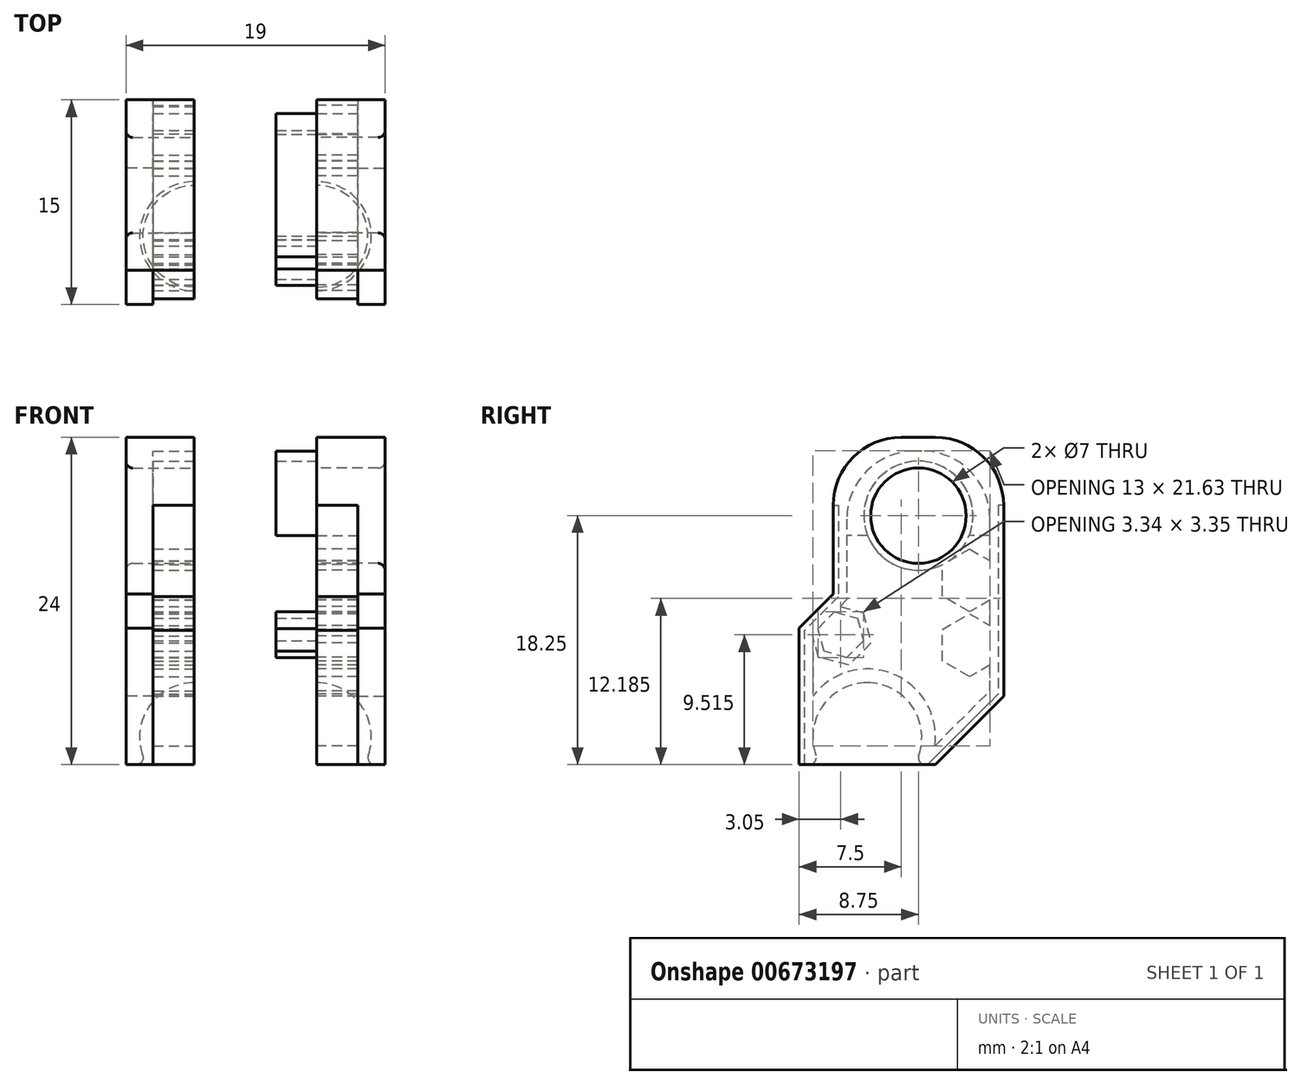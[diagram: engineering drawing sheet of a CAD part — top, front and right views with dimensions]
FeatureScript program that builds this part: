
annotation { "Feature Type Name" : "Feature", "Feature Type Description" : "" }
export const myFeature = defineFeature(function(context is Context, id is Id, definition is map)
    precondition{}
    {
        {
            var Q0;
            Q0=qCreatedBy(makeId("Right.planeOp"),FACE);
            var sketch = newSketch(context, id + "F0", { "sketchPlane" : qUnion([Q0])});
            skLineSegment(sketch, "E0.bottom", {"start": v(0, 0) * mm, "end": v(10, 0) * mm});
            skLineSegment(sketch, "E0.left", {"start": v(0, 0) * mm, "end": v(0, 10) * mm});
            skLineSegment(sketch, "E1.right", {"start": v(15, 5) * mm, "end": v(15, 20) * mm});
            skLineSegment(sketch, "E2", {"start": v(15, 5) * mm, "end": v(10, 0) * mm});
            skLineSegment(sketch, "E3", {"start": v(2.5, 12.5) * mm, "end": v(0, 10) * mm});
            skLineSegment(sketch, "E4", {"start": v(2.5, 12.5) * mm, "end": v(2.5, 20) * mm});
            skLineSegment(sketch, "E5.top", {"start": v(2.5, 24) * mm, "end": v(15, 24) * mm});
            skLineSegment(sketch, "E5.left", {"start": v(2.5, 20) * mm, "end": v(2.5, 24) * mm});
            skLineSegment(sketch, "E5.right", {"start": v(15, 20) * mm, "end": v(15, 24) * mm});
            skSolve(sketch);
        }
        {
            var Q0;
            Q0=qSketchRegion(id+"F0",true);
            extrude(context, id + "F1", {"entities" : qUnion([Q0]), "depth" : 5 * mm});
        }
        {
            var Q0;
            Q0=makeQuery(id+"F1.opExtrude","CAP_FACE",FACE,{"disambiguationData":[OSD([sQuery(id+"F0.wireOp",EDGE,"E0.bottom"),sQuery(id+"F0.wireOp",EDGE,"E0.left"),sQuery(id+"F0.wireOp",EDGE,"E1.top"),sQuery(id+"F0.wireOp",EDGE,"E1.right"),sQuery(id+"F0.wireOp",EDGE,"E2"),sQuery(id+"F0.wireOp",EDGE,"E3"),sQuery(id+"F0.wireOp",EDGE,"E4"),sQuery(id+"F0.wireOp",EDGE,"LedBFlpj-Cklq-8Npn-dqWy-Sleq267MBf9Z")])],"isStart":false});
            var sketch = newSketch(context, id + "F2", { "sketchPlane" : qUnion([Q0])});
            skLineSegment(sketch, "E6", {"start": v(5, 0) * mm, "end": v(5, 2) * mm, "construction": true});
            skArc(sketch, "E7", {"start": v(5, 6) * mm, "mid": v(1, 2) * mm, "end": v(5, -2) * mm});
            skLineSegment(sketch, "E8", {"start": v(5, 6) * mm, "end": v(5, -2) * mm});
            skSolve(sketch);
        }
        {
            var Q0;
            Q0=qSketchRegion(id+"F2",true);
            var Q1;
            Q1=sQuery(id+"F2.wireOp",EDGE,"E8");
            revolve(context, id + "F3", {"operationType" : NewBodyOperationType.REMOVE, "entities" : qUnion([Q0]), "axis" : qUnion([Q1]), "revolveType" : RevolveType.FULL, "oppositeDirection" : true});
        }
        {
            var Q0;
            Q0=makeQuery(id+"F1.opExtrude","CAP_FACE",FACE,{"disambiguationData":[OSD([sQuery(id+"F0.wireOp",EDGE,"E0.bottom"),sQuery(id+"F0.wireOp",EDGE,"E0.left"),sQuery(id+"F0.wireOp",EDGE,"E1.right"),sQuery(id+"F0.wireOp",EDGE,"E2"),sQuery(id+"F0.wireOp",EDGE,"E3"),sQuery(id+"F0.wireOp",EDGE,"E4"),sQuery(id+"F0.wireOp",EDGE,"E5.top"),sQuery(id+"F0.wireOp",EDGE,"E5.left"),sQuery(id+"F0.wireOp",EDGE,"E5.right")])],"isStart":false});
            var sketch = newSketch(context, id + "F4", { "sketchPlane" : qUnion([Q0])});
            skCircle(sketch, "E9", {"center": v(8.75, 18.25) * mm, "radius": 3.5 * mm});
            skPoint(sketch, "E9.centerSnap0", {"position": v(2.5, 18.25) * mm});
            skPoint(sketch, "E9.centerSnap1", {"position": v(8.75, 24) * mm});
            skSolve(sketch);
        }
        {
            var Q0;
            Q0=qSketchRegion(id+"F4",true);
            extrude(context, id + "F5", {"entities" : qUnion([Q0]), "operationType" : NewBodyOperationType.REMOVE, "oppositeDirection" : true, "depth" : 25 * mm});
        }
        {
            var Q0;
            Q0=makeQuery(id+"F1.opExtrude","CAP_FACE",FACE,{"disambiguationData":[OSD([sQuery(id+"F0.wireOp",EDGE,"E0.bottom"),sQuery(id+"F0.wireOp",EDGE,"E0.left"),sQuery(id+"F0.wireOp",EDGE,"E1.right"),sQuery(id+"F0.wireOp",EDGE,"E2"),sQuery(id+"F0.wireOp",EDGE,"E3"),sQuery(id+"F0.wireOp",EDGE,"E4"),sQuery(id+"F0.wireOp",EDGE,"E5.top"),sQuery(id+"F0.wireOp",EDGE,"E5.left"),sQuery(id+"F0.wireOp",EDGE,"E5.right")])],"isStart":false});
            var sketch = newSketch(context, id + "F6", { "sketchPlane" : qUnion([Q0])});
            skLineSegment(sketch, "E10.0", {"start": v(1, 9.59) * mm, "end": v(1, 5) * mm});
            skLineSegment(sketch, "E10.1", {"start": v(3.5, 12.09) * mm, "end": v(1, 9.59) * mm});
            skLineSegment(sketch, "E10.2", {"start": v(9.96, 1.37) * mm, "end": v(14, 5.41) * mm});
            skLineSegment(sketch, "E10.3", {"start": v(14, 5.41) * mm, "end": v(14, 23) * mm});
            skLineSegment(sketch, "E10.4", {"start": v(14, 23) * mm, "end": v(3.5, 23) * mm});
            skArc(sketch, "E10.5", {"start": v(1, 5) * mm, "mid": v(6.88, 6.64) * mm, "end": v(9.96, 1.37) * mm});
            skLineSegment(sketch, "E10.6", {"start": v(3.5, 23) * mm, "end": v(3.5, 12.09) * mm});
            skCircle(sketch, "E11.cCircle", {"center": v(12.5, 8.75) * mm, "radius": 1.5 * mm, "construction": true});
            skLineSegment(sketch, "E11.0", {"start": v(14, 9.61) * mm, "end": v(14, 7.88) * mm});
            skLineSegment(sketch, "E11.1", {"start": v(14, 7.88) * mm, "end": v(12.5, 7.01) * mm});
            skLineSegment(sketch, "E11.2", {"start": v(12.5, 7.01) * mm, "end": v(11, 7.88) * mm});
            skLineSegment(sketch, "E11.3", {"start": v(11, 7.88) * mm, "end": v(11, 9.61) * mm});
            skLineSegment(sketch, "E11.4", {"start": v(11, 9.61) * mm, "end": v(12.5, 10.48) * mm});
            skLineSegment(sketch, "E11.5", {"start": v(12.5, 10.48) * mm, "end": v(14, 9.61) * mm});
            skPoint(sketch, "E11.0.midPoint", {"position": v(14, 8.75) * mm});
            skCircle(sketch, "E12.cCircle", {"center": v(3.05, 9.52) * mm, "radius": 1.5 * mm, "construction": true});
            skLineSegment(sketch, "E12.0", {"start": v(1.38, 9.96) * mm, "end": v(2.6, 11.19) * mm});
            skLineSegment(sketch, "E12.1", {"start": v(2.6, 11.19) * mm, "end": v(4.28, 10.74) * mm});
            skLineSegment(sketch, "E12.2", {"start": v(4.28, 10.74) * mm, "end": v(4.72, 9.07) * mm});
            skLineSegment(sketch, "E12.3", {"start": v(4.72, 9.07) * mm, "end": v(3.5, 7.84) * mm});
            skLineSegment(sketch, "E12.4", {"start": v(3.5, 7.84) * mm, "end": v(1.83, 8.3) * mm});
            skLineSegment(sketch, "E12.5", {"start": v(1.83, 8.3) * mm, "end": v(1.38, 9.96) * mm});
            skPoint(sketch, "E12.0.midPoint", {"position": v(2, 10.58) * mm});
            skCircle(sketch, "E13.cCircle", {"center": v(12.5, 13.5) * mm, "radius": 1.5 * mm, "construction": true});
            skLineSegment(sketch, "E13.0", {"start": v(14, 14.37) * mm, "end": v(14, 12.63) * mm});
            skLineSegment(sketch, "E13.1", {"start": v(14, 12.63) * mm, "end": v(12.5, 11.77) * mm});
            skLineSegment(sketch, "E13.2", {"start": v(12.5, 11.77) * mm, "end": v(11, 12.63) * mm});
            skLineSegment(sketch, "E13.3", {"start": v(11, 12.63) * mm, "end": v(11, 14.37) * mm});
            skLineSegment(sketch, "E13.4", {"start": v(11, 14.37) * mm, "end": v(12.5, 15.23) * mm});
            skLineSegment(sketch, "E13.5", {"start": v(12.5, 15.23) * mm, "end": v(14, 14.37) * mm});
            skPoint(sketch, "E13.0.midPoint", {"position": v(14, 13.5) * mm});
            skCircle(sketch, "E14", {"center": v(8.75, 18.25) * mm, "radius": 4 * mm});
            skCircle(sketch, "E15.cCircle", {"center": v(12.5, 8.75) * mm, "radius": 2 * mm, "construction": true});
            skLineSegment(sketch, "E15.1", {"start": v(14, 7.3) * mm, "end": v(12.5, 6.44) * mm});
            skLineSegment(sketch, "E15.2", {"start": v(12.5, 6.44) * mm, "end": v(10.5, 7.6) * mm});
            skLineSegment(sketch, "E15.3", {"start": v(10.5, 7.6) * mm, "end": v(10.5, 9.9) * mm});
            skLineSegment(sketch, "E15.4", {"start": v(10.5, 9.9) * mm, "end": v(12.5, 11.06) * mm});
            skLineSegment(sketch, "E15.5", {"start": v(12.5, 11.06) * mm, "end": v(14, 10.19) * mm});
            skPoint(sketch, "E15.0.midPoint", {"position": v(14.5, 8.75) * mm});
            skCircle(sketch, "E16.cCircle", {"center": v(12.5, 13.5) * mm, "radius": 2 * mm, "construction": true});
            skLineSegment(sketch, "E16.1", {"start": v(14, 12.06) * mm, "end": v(12.5, 11.2) * mm});
            skLineSegment(sketch, "E16.2", {"start": v(12.5, 11.2) * mm, "end": v(10.5, 12.35) * mm});
            skLineSegment(sketch, "E16.3", {"start": v(10.5, 12.35) * mm, "end": v(10.5, 14.65) * mm});
            skLineSegment(sketch, "E16.4", {"start": v(10.5, 14.65) * mm, "end": v(12.5, 15.8) * mm});
            skLineSegment(sketch, "E16.5", {"start": v(12.5, 15.8) * mm, "end": v(14, 14.94) * mm});
            skPoint(sketch, "E16.0.midPoint", {"position": v(14.5, 13.5) * mm});
            skArc(sketch, "E17.cCircle", {"start": v(1.06, 9.64) * mm, "mid": v(4.47, 8.1) * mm, "end": v(2.93, 11.51) * mm, "construction": true});
            skLineSegment(sketch, "E17.1", {"start": v(3.01, 11.6) * mm, "end": v(4.68, 11.15) * mm});
            skLineSegment(sketch, "E17.2", {"start": v(4.68, 11.15) * mm, "end": v(5.28, 8.92) * mm});
            skLineSegment(sketch, "E17.3", {"start": v(5.28, 8.92) * mm, "end": v(3.65, 7.29) * mm});
            skLineSegment(sketch, "E17.4", {"start": v(3.65, 7.29) * mm, "end": v(1.42, 7.88) * mm});
            skLineSegment(sketch, "E17.5", {"start": v(1.42, 7.88) * mm, "end": v(1, 9.44) * mm});
            skPoint(sketch, "E17.0.midPoint", {"position": v(1.64, 10.93) * mm});
            skPoint(sketch, "E18.orphan", {"position": v(0.82, 10.11) * mm});
            skPoint(sketch, "E19.orphan", {"position": v(2.45, 11.75) * mm});
            skPoint(sketch, "E20.orphan", {"position": v(14.5, 7.6) * mm});
            skPoint(sketch, "E21.orphan", {"position": v(14.5, 9.9) * mm});
            skPoint(sketch, "E22.orphan", {"position": v(14.5, 12.35) * mm});
            skPoint(sketch, "E23.orphan", {"position": v(14.5, 14.65) * mm});
            skSolve(sketch);
        }
        {
            var Q0;
            {var subQ15=sQuery(id+"F6.wireOp",EDGE,"E10.2");Q0=makeQuery(id+"F6.imprint","IMPRINT",FACE,{"disambiguationData":[TD([[makeQuery(id+"F6.imprint","IMPRINT",EDGE,{"derivedFrom":subQ15}),1.0]])]});}
            var Q1;
            Q1=makeQuery(id+"F6.imprint","IMPRINT",FACE,{"disambiguationData":[TD([[makeQuery(id+"F6.imprint","IMPRINT",EDGE,{"derivedFrom":sQuery(id+"F6.wireOp",EDGE,"E12.0")}),-1.0]])]});
            var Q2;
            Q2=makeQuery(id+"F6.imprint","IMPRINT",FACE,{"disambiguationData":[TD([[makeQuery(id+"F6.imprint","IMPRINT",EDGE,{"derivedFrom":sQuery(id+"F6.wireOp",EDGE,"E11.0")}),-1.0]])]});
            var Q3;
            Q3=makeQuery(id+"F6.imprint","IMPRINT",FACE,{"disambiguationData":[TD([[makeQuery(id+"F6.imprint","IMPRINT",EDGE,{"derivedFrom":sQuery(id+"F6.wireOp",EDGE,"E13.0")}),-1.0]])]});
            extrude(context, id + "F7", {"entities" : qUnion([Q0, Q1, Q2, Q3]), "operationType" : NewBodyOperationType.REMOVE, "oppositeDirection" : true, "depth" : 3 * mm});
        }
        {
            var Q0;
            Q0=qCreatedBy(makeId("Right.planeOp"),FACE);
            cPlane(context, id + "F8", {"entities" : qUnion([Q0]), "cplaneType" : CPlaneType.OFFSET, "offset" : 9.5 * mm, "width" : 150 * mm, "height" : 150 * mm});
        }
        {
            var Q0;
            Q0=makeQuery(id+"F1.opExtrude","SWEPT_EDGE",EDGE,{"disambiguationData":[OSD([sQuery(id+"F0.wireOp",EDGE,"E5.top"),sQuery(id+"F0.wireOp",EDGE,"E5.left")])]});
            var Q1;
            Q1=makeQuery(id+"F1.opExtrude","SWEPT_EDGE",EDGE,{"disambiguationData":[OSD([sQuery(id+"F0.wireOp",EDGE,"E5.top"),sQuery(id+"F0.wireOp",EDGE,"E5.right")])]});
            var Q2;
            Q2=makeQuery(id+"F7.boolean.opBoolean","COPY",EDGE,{"derivedFrom":makeQuery(id+"F7.opExtrude","SWEPT_EDGE",EDGE,{"disambiguationData":[OSD([sQuery(id+"F6.wireOp",EDGE,"E10.4"),sQuery(id+"F6.wireOp",EDGE,"E10.6")])]})});
            var Q3;
            Q3=makeQuery(id+"F7.boolean.opBoolean","COPY",EDGE,{"derivedFrom":makeQuery(id+"F7.opExtrude","SWEPT_EDGE",EDGE,{"disambiguationData":[OSD([sQuery(id+"F6.wireOp",EDGE,"E10.3"),sQuery(id+"F6.wireOp",EDGE,"E10.4")])]})});
            fillet(context, id + "F9", {"entities" : qUnion([Q0, Q1, Q2, Q3]), "radius" : 5 * mm, "tangentPropagation" : true, "allowEdgeOverflow" : false});
        }
        {
            var Q0;
            Q0=makeQuery(id+"F1.opExtrude","SWEPT_BODY",BODY,{"disambiguationData":[OSD([sQuery(id+"F0.wireOp",EDGE,"E0.bottom"),sQuery(id+"F0.wireOp",EDGE,"E0.left"),sQuery(id+"F0.wireOp",EDGE,"E1.right"),sQuery(id+"F0.wireOp",EDGE,"E2"),sQuery(id+"F0.wireOp",EDGE,"E3"),sQuery(id+"F0.wireOp",EDGE,"E4"),sQuery(id+"F0.wireOp",EDGE,"E5.top"),sQuery(id+"F0.wireOp",EDGE,"E5.left"),sQuery(id+"F0.wireOp",EDGE,"E5.right")])]});
            var Q1;
            Q1=qCreatedBy(id+"F8.planeOp",FACE);
            mirror(context, id + "F10", {"entities" : qUnion([Q0]), "mirrorPlane" : qUnion([Q1])});
        }
        {
            var Q0;
            Q0=makeQuery(id+"F10.opPattern","COPY",FACE,{"derivedFrom":makeQuery(id+"F7.boolean.opBoolean","COPY",FACE,{"derivedFrom":makeQuery(id+"F7.opExtrude","CAP_FACE",FACE,{"disambiguationData":[OSD([sQuery(id+"F6.wireOp",EDGE,"E11.0"),sQuery(id+"F6.wireOp",EDGE,"E11.1"),sQuery(id+"F6.wireOp",EDGE,"E11.2"),sQuery(id+"F6.wireOp",EDGE,"E11.3"),sQuery(id+"F6.wireOp",EDGE,"E11.4"),sQuery(id+"F6.wireOp",EDGE,"E11.5")])],"isStart":false})}),"instanceName":"1"});
            var Q1;
            Q1=makeQuery(id+"F10.opPattern","COPY",FACE,{"derivedFrom":makeQuery(id+"F7.boolean.opBoolean","COPY",FACE,{"derivedFrom":makeQuery(id+"F7.opExtrude","CAP_FACE",FACE,{"disambiguationData":[OSD([sQuery(id+"F6.wireOp",EDGE,"E13.0"),sQuery(id+"F6.wireOp",EDGE,"E13.1"),sQuery(id+"F6.wireOp",EDGE,"E13.2"),sQuery(id+"F6.wireOp",EDGE,"E13.3"),sQuery(id+"F6.wireOp",EDGE,"E13.4"),sQuery(id+"F6.wireOp",EDGE,"E13.5")])],"isStart":false})}),"instanceName":"1"});
            var Q2;
            Q2=makeQuery(id+"F10.opPattern","COPY",FACE,{"derivedFrom":makeQuery(id+"F7.boolean.opBoolean","COPY",FACE,{"derivedFrom":makeQuery(id+"F7.opExtrude","CAP_FACE",FACE,{"disambiguationData":[OSD([sQuery(id+"F6.wireOp",EDGE,"E12.0"),sQuery(id+"F6.wireOp",EDGE,"E12.1"),sQuery(id+"F6.wireOp",EDGE,"E12.2"),sQuery(id+"F6.wireOp",EDGE,"E12.3"),sQuery(id+"F6.wireOp",EDGE,"E12.4"),sQuery(id+"F6.wireOp",EDGE,"E12.5")])],"isStart":false})}),"instanceName":"1"});
            extrude(context, id + "F11", {"entities" : qUnion([Q0, Q1, Q2]), "operationType" : NewBodyOperationType.ADD, "depth" : 6 * mm});
        }
        {
            var Q0;
            Q0=makeQuery(id+"F10.opPattern","COPY",FACE,{"derivedFrom":makeQuery(id+"F7.boolean.opBoolean","COPY",FACE,{"derivedFrom":makeQuery(id+"F7.opExtrude","CAP_FACE",FACE,{"disambiguationData":[OSD([sQuery(id+"F6.wireOp",EDGE,"E10.0"),sQuery(id+"F6.wireOp",EDGE,"E10.1"),sQuery(id+"F6.wireOp",EDGE,"E10.2"),sQuery(id+"F6.wireOp",EDGE,"E10.3"),sQuery(id+"F6.wireOp",EDGE,"E10.4"),sQuery(id+"F6.wireOp",EDGE,"E10.5"),sQuery(id+"F6.wireOp",EDGE,"E10.6"),sQuery(id+"F6.wireOp",EDGE,"E14"),sQuery(id+"F6.wireOp",EDGE,"E15.1"),sQuery(id+"F6.wireOp",EDGE,"E15.2"),sQuery(id+"F6.wireOp",EDGE,"E15.3"),sQuery(id+"F6.wireOp",EDGE,"E15.4"),sQuery(id+"F6.wireOp",EDGE,"E15.5"),sQuery(id+"F6.wireOp",EDGE,"E16.1"),sQuery(id+"F6.wireOp",EDGE,"E16.2"),sQuery(id+"F6.wireOp",EDGE,"E16.3"),sQuery(id+"F6.wireOp",EDGE,"E16.4"),sQuery(id+"F6.wireOp",EDGE,"E16.5"),sQuery(id+"F6.wireOp",EDGE,"E17.1"),sQuery(id+"F6.wireOp",EDGE,"E17.2"),sQuery(id+"F6.wireOp",EDGE,"E17.3"),sQuery(id+"F6.wireOp",EDGE,"E17.4"),sQuery(id+"F6.wireOp",EDGE,"E17.5")])],"isStart":false})}),"instanceName":"1"});
            var sketch = newSketch(context, id + "F12", { "sketchPlane" : qUnion([Q0])});
            skLineSegment(sketch, "E24", {"start": v(-14, 15.8) * mm, "end": v(-14, 16.8) * mm, "construction": true});
            skLineSegment(sketch, "E25", {"start": v(-14, 16.8) * mm, "end": v(-12.48, 16.8) * mm});
            skLineSegment(sketch, "E26", {"start": v(-12.48, 16.8) * mm, "end": v(-3.5, 16.8) * mm});
            skSolve(sketch);
        }
        {
            var Q0;
            {var subQ14=sQuery(id+"F12.wireOp",EDGE,"E25");Q0=makeQuery(id+"F12.imprint","IMPRINT",FACE,{"disambiguationData":[TD([[makeQuery(id+"F12.imprint","IMPRINT",EDGE,{"derivedFrom":subQ14}),1.0]])]});}
            extrude(context, id + "F13", {"entities" : qUnion([Q0]), "operationType" : NewBodyOperationType.ADD, "depth" : 6 * mm});
        }
        {
            var Q0;
            Q0=makeQuery(id+"F5.boolean.opBoolean","INTERSECT",EDGE,{"derivedFrom":[makeQuery(id+"F1.opExtrude","CAP_FACE",FACE,{"disambiguationData":[OSD([sQuery(id+"F0.wireOp",EDGE,"E0.bottom"),sQuery(id+"F0.wireOp",EDGE,"E0.left"),sQuery(id+"F0.wireOp",EDGE,"E1.right"),sQuery(id+"F0.wireOp",EDGE,"E2"),sQuery(id+"F0.wireOp",EDGE,"E3"),sQuery(id+"F0.wireOp",EDGE,"E4"),sQuery(id+"F0.wireOp",EDGE,"E5.top"),sQuery(id+"F0.wireOp",EDGE,"E5.left"),sQuery(id+"F0.wireOp",EDGE,"E5.right")])],"isStart":true}),makeQuery(id+"F5.opExtrude","SWEPT_FACE",FACE,{"disambiguationData":[OSD([sQuery(id+"F4.wireOp",EDGE,"E9")])]})]});
            var Q1;
            Q1=makeQuery(id+"F10.opPattern","COPY",EDGE,{"derivedFrom":makeQuery(id+"F5.boolean.opBoolean","INTERSECT",EDGE,{"derivedFrom":[makeQuery(id+"F1.opExtrude","CAP_FACE",FACE,{"disambiguationData":[OSD([sQuery(id+"F0.wireOp",EDGE,"E0.bottom"),sQuery(id+"F0.wireOp",EDGE,"E0.left"),sQuery(id+"F0.wireOp",EDGE,"E1.right"),sQuery(id+"F0.wireOp",EDGE,"E2"),sQuery(id+"F0.wireOp",EDGE,"E3"),sQuery(id+"F0.wireOp",EDGE,"E4"),sQuery(id+"F0.wireOp",EDGE,"E5.top"),sQuery(id+"F0.wireOp",EDGE,"E5.left"),sQuery(id+"F0.wireOp",EDGE,"E5.right")])],"isStart":true}),makeQuery(id+"F5.opExtrude","SWEPT_FACE",FACE,{"disambiguationData":[OSD([sQuery(id+"F4.wireOp",EDGE,"E9")])]})]}),"instanceName":"1"});
            var Q2;
            Q2=makeQuery(id+"F10.opPattern","COPY",EDGE,{"derivedFrom":makeQuery(id+"F3.boolean.opBoolean","INTERSECT",EDGE,{"derivedFrom":[makeQuery(id+"F1.opExtrude","SWEPT_FACE",FACE,{"disambiguationData":[OSD([sQuery(id+"F0.wireOp",EDGE,"E0.bottom")])]}),makeQuery(id+"F3.opRevolve","SWEPT_FACE",FACE,{"disambiguationData":[OSD([sQuery(id+"F2.wireOp",EDGE,"E7")])]})]}),"instanceName":"1"});
            var Q3;
            Q3=makeQuery(id+"F3.boolean.opBoolean","INTERSECT",EDGE,{"derivedFrom":[makeQuery(id+"F1.opExtrude","SWEPT_FACE",FACE,{"disambiguationData":[OSD([sQuery(id+"F0.wireOp",EDGE,"E0.bottom")])]}),makeQuery(id+"F3.opRevolve","SWEPT_FACE",FACE,{"disambiguationData":[OSD([sQuery(id+"F2.wireOp",EDGE,"E7")])]})]});
            fillet(context, id + "F14", {"entities" : qUnion([Q0, Q1, Q2, Q3]), "radius" : .5 * mm, "tangentPropagation" : true, "allowEdgeOverflow" : false});
        }
        {
            var Q0;
            Q0=makeQuery(id+"F1.opExtrude","CAP_FACE",FACE,{"disambiguationData":[OSD([sQuery(id+"F0.wireOp",EDGE,"E0.bottom"),sQuery(id+"F0.wireOp",EDGE,"E0.left"),sQuery(id+"F0.wireOp",EDGE,"E1.right"),sQuery(id+"F0.wireOp",EDGE,"E2"),sQuery(id+"F0.wireOp",EDGE,"E3"),sQuery(id+"F0.wireOp",EDGE,"E4"),sQuery(id+"F0.wireOp",EDGE,"E5.top"),sQuery(id+"F0.wireOp",EDGE,"E5.left"),sQuery(id+"F0.wireOp",EDGE,"E5.right")])],"isStart":false});
            var sketch = newSketch(context, id + "F15", { "sketchPlane" : qUnion([Q0])});
            skLineSegment(sketch, "E27", {"start": v(0, 0) * mm, "end": v(0.4, 0) * mm});
            skLineSegment(sketch, "E28", {"start": v(0.4, 0) * mm, "end": v(0.4, 9.83) * mm});
            skLineSegment(sketch, "E29", {"start": v(2.89, 12.32) * mm, "end": v(0.4, 9.83) * mm});
            skLineSegment(sketch, "E30", {"start": v(2.9, 19) * mm, "end": v(2.9, 12.82) * mm});
            skLineSegment(sketch, "E31", {"start": v(2.89, 12.32) * mm, "end": v(2.9, 12.33) * mm});
            skLineSegment(sketch, "E32", {"start": v(2.9, 12.82) * mm, "end": v(2.9, 12.33) * mm});
            skLineSegment(sketch, "E33", {"start": v(2.9, 19) * mm, "end": v(2.5, 19) * mm});
            skLineSegment(sketch, "E34", {"start": v(14.52, 5.08) * mm, "end": v(9.43, 0) * mm});
            skLineSegment(sketch, "E35", {"start": v(10, 0) * mm, "end": v(9.43, 0) * mm});
            skLineSegment(sketch, "E36", {"start": v(14.6, 19) * mm, "end": v(14.6, 5.17) * mm});
            skLineSegment(sketch, "E37", {"start": v(14.52, 5.08) * mm, "end": v(14.6, 5.17) * mm});
            skLineSegment(sketch, "E38", {"start": v(14.6, 19) * mm, "end": v(15, 19) * mm});
            skSolve(sketch);
        }
        {
            var Q0;
            Q0=makeQuery(id+"F15.imprint","IMPRINT",FACE,{"disambiguationData":[TD([[makeQuery(id+"F15.imprint","IMPRINT",EDGE,{"derivedFrom":sQuery(id+"F15.wireOp",EDGE,"E27")}),1.0]])]});
            var Q1;
            Q1=makeQuery(id+"F15.imprint","IMPRINT",FACE,{"disambiguationData":[TD([[makeQuery(id+"F15.imprint","IMPRINT",EDGE,{"derivedFrom":sQuery(id+"F15.wireOp",EDGE,"E34")}),1.0]])]});
            extrude(context, id + "F16", {"entities" : qUnion([Q0, Q1]), "operationType" : NewBodyOperationType.REMOVE, "oppositeDirection" : true, "depth" : 3 * mm});
        }
        {
            var Q0;
            Q0=makeQuery(id+"F10.opPattern","COPY",FACE,{"derivedFrom":makeQuery(id+"F1.opExtrude","CAP_FACE",FACE,{"disambiguationData":[OSD([sQuery(id+"F0.wireOp",EDGE,"E0.bottom"),sQuery(id+"F0.wireOp",EDGE,"E0.left"),sQuery(id+"F0.wireOp",EDGE,"E1.right"),sQuery(id+"F0.wireOp",EDGE,"E2"),sQuery(id+"F0.wireOp",EDGE,"E3"),sQuery(id+"F0.wireOp",EDGE,"E4"),sQuery(id+"F0.wireOp",EDGE,"E5.top"),sQuery(id+"F0.wireOp",EDGE,"E5.left"),sQuery(id+"F0.wireOp",EDGE,"E5.right")])],"isStart":false}),"instanceName":"1"});
            var sketch = newSketch(context, id + "F17", { "sketchPlane" : qUnion([Q0])});
            skLineSegment(sketch, "E39", {"start": v(0, 0) * mm, "end": v(-0.4, 0) * mm});
            skLineSegment(sketch, "E40", {"start": v(-0.4, 0) * mm, "end": v(-0.4, 9.83) * mm});
            skLineSegment(sketch, "E41", {"start": v(-2.9, 12.33) * mm, "end": v(-0.4, 9.83) * mm});
            skLineSegment(sketch, "E42", {"start": v(-2.5, 19) * mm, "end": v(-2.9, 19) * mm});
            skLineSegment(sketch, "E43", {"start": v(-2.9, 19) * mm, "end": v(-2.9, 12.33) * mm});
            skLineSegment(sketch, "E44", {"start": v(-15, 19) * mm, "end": v(-14.6, 19) * mm});
            skLineSegment(sketch, "E45", {"start": v(-14.6, 19) * mm, "end": v(-14.6, 5.17) * mm});
            skLineSegment(sketch, "E46", {"start": v(-10, 0) * mm, "end": v(-9.43, 0) * mm});
            skLineSegment(sketch, "E47", {"start": v(-9.43, 0) * mm, "end": v(-14.6, 5.17) * mm});
            skSolve(sketch);
        }
        {
            var Q0;
            Q0=qSketchRegion(id+"F17",true);
            var Q1;
            Q1=makeQuery(id+"F17.imprint","IMPRINT",FACE,{"disambiguationData":[TD([[makeQuery(id+"F17.imprint","IMPRINT",EDGE,{"derivedFrom":sQuery(id+"F17.wireOp",EDGE,"E44")}),-1.0]])]});
            var Q2;
            Q2=makeQuery(id+"F17.imprint","IMPRINT",FACE,{"disambiguationData":[TD([[makeQuery(id+"F17.imprint","IMPRINT",EDGE,{"derivedFrom":sQuery(id+"F17.wireOp",EDGE,"E39")}),-1.0]])]});
            extrude(context, id + "F18", {"entities" : qUnion([Q0, Q1, Q2]), "operationType" : NewBodyOperationType.REMOVE, "oppositeDirection" : true, "depth" : 3 * mm});
        }
    });
